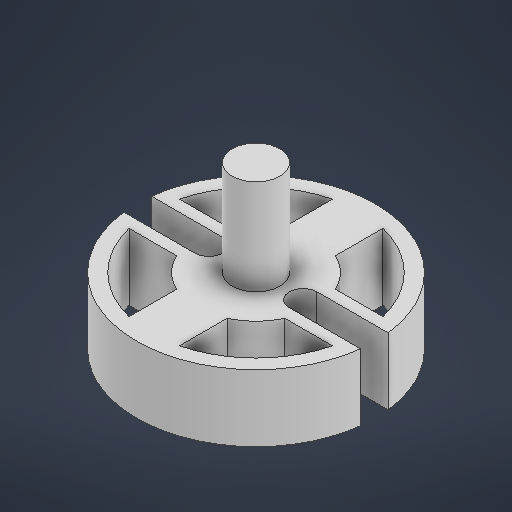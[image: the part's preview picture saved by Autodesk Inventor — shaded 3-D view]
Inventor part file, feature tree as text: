
AUTODESK INVENTOR PART (.ipt)
format: ipt  version: 2025.3 (Build 293356000, 356)  size: 280,576 bytes
history: native  units: mm
features: sketch x5, extrude x4, plane x2
ambient origin geometry x8: Origin, YZ Plane, XZ Plane, XY Plane, X Axis, Y Axis, Z Axis, Center Point
bodies: Solid1 (feature_tree)
feature tree (11):
  extrude  "Extrusion1"  Depth=10.0mm
  extrude  "Extrusion2"  Depth=10.0mm
  plane  "Work Plane3"
  extrude  "Extrusion4"  Depth=22.0mm
  plane  "Work Plane4"
  extrude  "Extrusion5"  Depth=14.0mm TaperAngle=0.0deg
  sketch  "Sketch1"  dims[d0=50.0mm d1=10.0mm]
  sketch  "Sketch2"  dims[d10=14.0mm d11=0.0mm d30=10.0mm]
  sketch  "Sketch Circular Pattern3"  dims[d31=6.981317mm d32=22.0mm]
  sketch  "Sketch4"  dims[d33=40.0mm d35=360.0deg d40=14.0mm d41=0.0mm]
  sketch  "Sketch6"  dims[d49=5.8mm d50=7.0mm d51=15.0mm d52=3.8mm d53=7.0mm d54=2.9mm d55=6.0mm d56=0.0mm d57=0.0mm d58=13.0mm d59=20.0mm d60=0.0mm d61=4.0mm d62=0.0mm]
